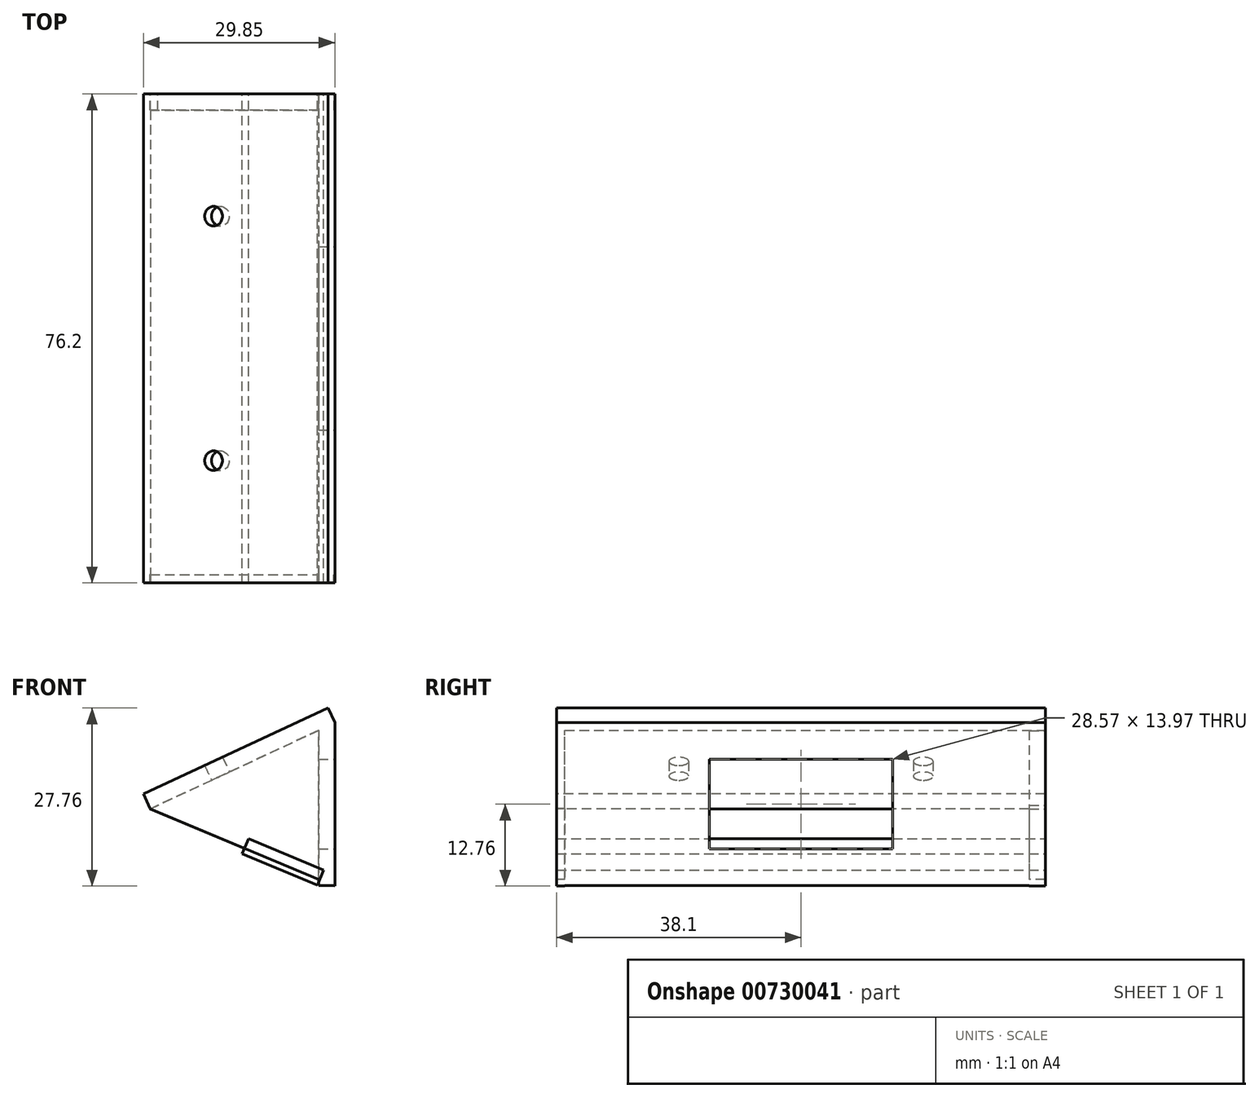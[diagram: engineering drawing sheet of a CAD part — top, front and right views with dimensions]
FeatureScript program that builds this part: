
annotation { "Feature Type Name" : "Feature", "Feature Type Description" : "" }
export const myFeature = defineFeature(function(context is Context, id is Id, definition is map)
    precondition{}
    {
        {
            var Q0;
            Q0=qCreatedBy(makeId("Right.planeOp"),FACE);
            var sketch = newSketch(context, id + "F0", { "sketchPlane" : qUnion([Q0])});
            skLineSegment(sketch, "E0.bottom", {"start": v(14.29, 6.99) * mm, "end": v(-14.29, 6.99) * mm});
            skLineSegment(sketch, "E0.top", {"start": v(14.29, -6.99) * mm, "end": v(-14.29, -6.99) * mm});
            skLineSegment(sketch, "E0.left", {"start": v(14.29, 6.99) * mm, "end": v(14.29, -6.99) * mm});
            skLineSegment(sketch, "E0.right", {"start": v(-14.29, 6.99) * mm, "end": v(-14.29, -6.99) * mm});
            skPoint(sketch, "E0.middle", {"position": v(0, 0) * mm});
            skLineSegment(sketch, "E1.bottom", {"start": v(38.1, 12.7) * mm, "end": v(-38.1, 12.7) * mm});
            skLineSegment(sketch, "E1.top", {"start": v(38.1, -12.7) * mm, "end": v(-38.1, -12.7) * mm});
            skLineSegment(sketch, "E1.left", {"start": v(38.1, 12.7) * mm, "end": v(38.1, -12.7) * mm});
            skLineSegment(sketch, "E1.right", {"start": v(-38.1, 12.7) * mm, "end": v(-38.1, -12.7) * mm});
            skSolve(sketch);
        }
        {
            var Q0;
            Q0=qCreatedBy(makeId("Top.planeOp"),FACE);
            var Q1;
            Q1=sQuery(id+"F0.wireOp",EDGE,"E1.bottom");
            cPlane(context, id + "F1", {"entities" : qUnion([Q0, Q1]), "cplaneType" : CPlaneType.LINE_ANGLE, "offset" : 25.4 * mm, "angle" : 25 * degree, "width" : 152.4 * mm, "height" : 152.4 * mm});
        }
        {
            var Q0;
            Q0=qCreatedBy(id+"F1.planeOp",FACE);
            var sketch = newSketch(context, id + "F2", { "sketchPlane" : qUnion([Q0])});
            skLineSegment(sketch, "E2.bottom", {"start": v(5.37, -38.1) * mm, "end": v(-26.38, -38.1) * mm});
            skLineSegment(sketch, "E2.top", {"start": v(5.37, 38.1) * mm, "end": v(-26.38, 38.1) * mm});
            skLineSegment(sketch, "E2.left", {"start": v(5.37, -38.1) * mm, "end": v(5.37, 38.1) * mm});
            skLineSegment(sketch, "E2.right", {"start": v(-26.38, -38.1) * mm, "end": v(-26.38, 38.1) * mm});
            skPoint(sketch, "E3", {"position": v(-14.32, 19.05) * mm});
            skPoint(sketch, "E4", {"position": v(-14.32, -19.05) * mm});
            skSolve(sketch);
        }
        {
            var Q0;
            Q0=qCreatedBy(makeId("Front.planeOp"),FACE);
            cPlane(context, id + "F3", {"entities" : qUnion([Q0]), "cplaneType" : CPlaneType.OFFSET, "offset" : 38.1 * mm, "width" : 152.4 * mm, "height" : 152.4 * mm});
        }
        {
            var Q0;
            Q0=qCreatedBy(makeId("Front.planeOp"),FACE);
            cPlane(context, id + "F4", {"entities" : qUnion([Q0]), "cplaneType" : CPlaneType.OFFSET, "offset" : 38.1 * mm, "oppositeDirection" : true, "width" : 152.4 * mm, "height" : 152.4 * mm});
        }
        {
            var Q0;
            Q0=qCreatedBy(id+"F4.planeOp",FACE);
            var sketch = newSketch(context, id + "F5", { "sketchPlane" : qUnion([Q0])});
            skLineSegment(sketch, "E5", {"start": v(0, 12.66) * mm, "end": v(-28.83, -0.74) * mm});
            skLineSegment(sketch, "E6", {"start": v(-28.83, -0.74) * mm, "end": v(0, -12.76) * mm});
            skLineSegment(sketch, "E7", {"start": v(0, -12.76) * mm, "end": v(0, 12.66) * mm});
            skSolve(sketch);
        }
        {
            var Q0;
            Q0=qCreatedBy(id+"F3.planeOp",FACE);
            var sketch = newSketch(context, id + "F6", { "sketchPlane" : qUnion([Q0])});
            skLineSegment(sketch, "E8", {"start": v(0, 12.74) * mm, "end": v(-28.86, -0.68) * mm});
            skLineSegment(sketch, "E9", {"start": v(-28.86, -0.68) * mm, "end": v(0, -12.76) * mm});
            skLineSegment(sketch, "E10", {"start": v(0, -12.76) * mm, "end": v(0, 12.74) * mm});
            skSolve(sketch);
        }
        {
            var Q0;
            Q0 = qSketchRegion(id + "F6", true);
            extrude(context, id + "F7", {"entities" : qUnion([Q0]), "oppositeDirection" : true, "depth" : 1.27 * mm, "offsetDistance" : 25.4 * mm});
        }
        {
            var Q0;
            Q0 = qSketchRegion(id + "F6", true);
            extrude(context, id + "F8", {"entities" : qUnion([Q0]), "operationType" : NewBodyOperationType.ADD, "oppositeDirection" : true, "depth" : 1.27 * mm, "offsetDistance" : 25.4 * mm});
        }
        {
            var Q0;
            Q0=makeQuery(id+"F0.imprint","IMPRINT",FACE,{"disambiguationData":[TD([[makeQuery(id+"F0.imprint","IMPRINT",EDGE,{"derivedFrom":sQuery(id+"F0.wireOp",EDGE,"E0.bottom")}),-1.0]])]});
            extrude(context, id + "F9", {"entities" : qUnion([Q0]), "operationType" : NewBodyOperationType.ADD, "oppositeDirection" : true, "depth" : 2.54 * mm, "offsetDistance" : 25.4 * mm});
        }
        {
            var Q0;
            Q0=makeQuery(id+"F2.imprint","IMPRINT",FACE,{"disambiguationData":[TD([[makeQuery(id+"F2.imprint","IMPRINT",EDGE,{"derivedFrom":sQuery(id+"F2.wireOp",EDGE,"E2.bottom")}),-1.0]])]});
            extrude(context, id + "F10", {"entities" : qUnion([Q0]), "operationType" : NewBodyOperationType.ADD, "oppositeDirection" : true, "depth" : 2.54 * mm, "offsetDistance" : 25.4 * mm});
        }
        {
            var Q0;
            Q0=makeQuery(id+"F5.imprint","IMPRINT",FACE,{"disambiguationData":[TD([[makeQuery(id+"F5.imprint","IMPRINT",EDGE,{"derivedFrom":sQuery(id+"F5.wireOp",EDGE,"E5")}),1.0]])]});
            extrude(context, id + "F11", {"entities" : qUnion([Q0]), "operationType" : NewBodyOperationType.ADD, "depth" : 2.54 * mm, "offsetDistance" : 25.4 * mm});
        }
        {
            var Q0;
            Q0=sQuery(id+"F2.wireOp",VERTEX,"E3");
            var Q1;
            Q1=sQuery(id+"F2.wireOp",VERTEX,"E4");
            var Q2;
            Q2=makeQuery(id+"F7.opExtrude","SWEPT_BODY",BODY,{"disambiguationData":[OSD([sQuery(id+"F6.wireOp",EDGE,"E8"),sQuery(id+"F6.wireOp",EDGE,"E9"),sQuery(id+"F6.wireOp",EDGE,"E10")])]});
            hole(context, id + "F12", {"style" : HoleStyle.SIMPLE, "endStyle" : HoleEndStyle.THROUGH, "holeDiameter" : 3.05 * mm, "majorDiameter" : 6.35 * mm, "isTappedThrough" : true, "tappedDepth" : 12.7 * mm, "tapClearance" : 3, "locations" : qUnion([Q0, Q1]), "scope" : qUnion([Q2])});
        }
        {
            var Q0;
            Q0=qCreatedBy(makeId("Top.planeOp"),FACE);
            var Q1;
            Q1=makeQuery(id+"F9.opExtrude","CAP_EDGE",EDGE,{"disambiguationData":[OSD([sQuery(id+"F0.wireOp",EDGE,"E1.top")])],"isStart":false});
            cPlane(context, id + "F13", {"entities" : qUnion([Q0, Q1]), "cplaneType" : CPlaneType.LINE_ANGLE, "offset" : 25.4 * mm, "angle" : 22.68 * degree, "oppositeDirection" : true, "width" : 152.4 * mm, "height" : 152.4 * mm});
        }
        {
            var Q0;
            Q0=qCreatedBy(id+"F13.planeOp",FACE);
            var sketch = newSketch(context, id + "F14", { "sketchPlane" : qUnion([Q0])});
            skLineSegment(sketch, "E11.bottom", {"start": v(2.36, 38.1) * mm, "end": v(-10.34, 38.1) * mm});
            skLineSegment(sketch, "E11.top", {"start": v(2.36, -38.1) * mm, "end": v(-10.34, -38.1) * mm});
            skLineSegment(sketch, "E11.left", {"start": v(2.36, 38.1) * mm, "end": v(2.36, -38.1) * mm});
            skLineSegment(sketch, "E11.right", {"start": v(-10.34, 38.1) * mm, "end": v(-10.34, -38.1) * mm});
            skSolve(sketch);
        }
        {
            var Q0;
            Q0 = qSketchRegion(id + "F14", true);
            extrude(context, id + "F15", {"entities" : qUnion([Q0]), "oppositeDirection" : true, "depth" : 2.54 * mm, "offsetDistance" : 25.4 * mm});
        }
    });
